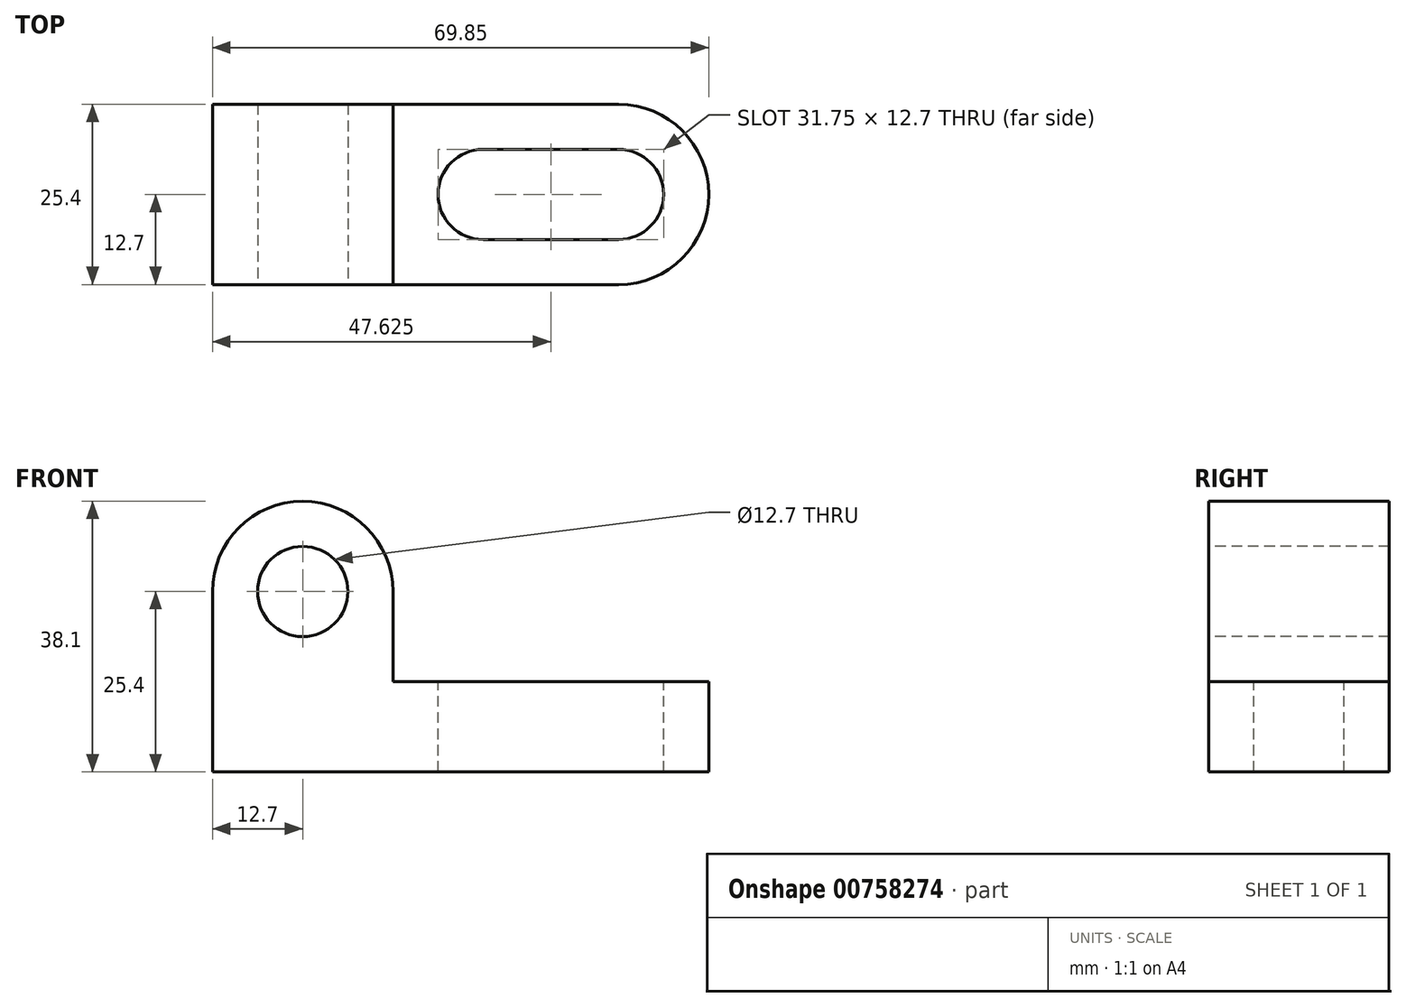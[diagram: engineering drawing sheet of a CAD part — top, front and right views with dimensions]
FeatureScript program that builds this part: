
annotation { "Feature Type Name" : "Feature", "Feature Type Description" : "" }
export const myFeature = defineFeature(function(context is Context, id is Id, definition is map)
    precondition{}
    {
        {
            var Q0;
            Q0=qCreatedBy(makeId("Front.planeOp"),FACE);
            var sketch = newSketch(context, id + "F0", { "sketchPlane" : qUnion([Q0])});
            skLineSegment(sketch, "E0", {"start": v(0, 0) * mm, "end": v(69.85, 0) * mm});
            skLineSegment(sketch, "E1", {"start": v(69.85, 0) * mm, "end": v(69.85, 38.1) * mm});
            skLineSegment(sketch, "E2", {"start": v(69.85, 38.1) * mm, "end": v(0, 38.1) * mm});
            skLineSegment(sketch, "E3", {"start": v(0, 38.1) * mm, "end": v(0, 0) * mm});
            skSolve(sketch);
        }
        {
            var Q0;
            Q0=makeQuery(id+"F0.imprint","IMPRINT",FACE,{"disambiguationData":[TD([[makeQuery(id+"F0.imprint","IMPRINT",EDGE,{"derivedFrom":sQuery(id+"F0.wireOp",EDGE,"E0")}),1.0]])]});
            extrude(context, id + "F1", {"entities" : qUnion([Q0]), "depth" : 25.4 * mm, "offsetDistance" : 25.4 * mm});
        }
        {
            var Q0;
            Q0=makeQuery(id+"F1.opExtrude","CAP_FACE",FACE,{"disambiguationData":[OSD([sQuery(id+"F0.wireOp",EDGE,"E0"),sQuery(id+"F0.wireOp",EDGE,"E1"),sQuery(id+"F0.wireOp",EDGE,"E2"),sQuery(id+"F0.wireOp",EDGE,"E3")])],"isStart":false});
            var sketch = newSketch(context, id + "F2", { "sketchPlane" : qUnion([Q0])});
            skLineSegment(sketch, "E4", {"start": v(25.4, 38.1) * mm, "end": v(25.4, 12.7) * mm});
            skLineSegment(sketch, "E5", {"start": v(25.4, 12.7) * mm, "end": v(69.85, 12.7) * mm});
            skSolve(sketch);
        }
        {
            var Q0;
            {var subQ0=sQuery(id+"F2.wireOp",EDGE,"E4");Q0=makeQuery(id+"F2.imprint","IMPRINT",FACE,{"disambiguationData":[TD([[makeQuery(id+"F2.imprint","IMPRINT",EDGE,{"derivedFrom":subQ0}),1.0]])]});}
            extrude(context, id + "F3", {"entities" : qUnion([Q0]), "operationType" : NewBodyOperationType.REMOVE, "oppositeDirection" : true, "depth" : 25.4 * mm, "offsetDistance" : 25.4 * mm});
        }
        {
            var Q0;
            Q0=makeQuery(id+"F3.boolean.opBoolean","COPY",FACE,{"derivedFrom":makeQuery(id+"F3.opExtrude","SWEPT_FACE",FACE,{"disambiguationData":[OSD([sQuery(id+"F2.wireOp",EDGE,"E5")])]})});
            var sketch = newSketch(context, id + "F4", { "sketchPlane" : qUnion([Q0])});
            skCircle(sketch, "E6", {"center": v(38.1, -12.7) * mm, "radius": 6.35 * mm});
            skPoint(sketch, "E6.centerSnap0", {"position": v(25.4, -12.7) * mm});
            skCircle(sketch, "E7", {"center": v(57.15, -12.7) * mm, "radius": 6.35 * mm});
            skLineSegment(sketch, "E8", {"start": v(38.1, -12.7) * mm, "end": v(38.1, -6.35) * mm});
            skLineSegment(sketch, "E9", {"start": v(38.1, -6.35) * mm, "end": v(57.15, -6.35) * mm});
            skLineSegment(sketch, "E10", {"start": v(57.15, -6.35) * mm, "end": v(57.15, -19.05) * mm});
            skLineSegment(sketch, "E11", {"start": v(57.15, -19.05) * mm, "end": v(38.1, -19.05) * mm});
            skLineSegment(sketch, "E12", {"start": v(38.1, -19.05) * mm, "end": v(38.1, -12.7) * mm});
            skSolve(sketch);
        }
        {
            var Q0;
            {var subQ0=sQuery(id+"F4.wireOp",EDGE,"E8");Q0=makeQuery(id+"F4.imprint","IMPRINT",FACE,{"disambiguationData":[TD([[makeQuery(id+"F4.imprint","IMPRINT",EDGE,{"derivedFrom":subQ0}),1.0]])]});}
            var Q1;
            {var subQ0=sQuery(id+"F4.wireOp",EDGE,"E8");Q1=makeQuery(id+"F4.imprint","IMPRINT",FACE,{"disambiguationData":[TD([[makeQuery(id+"F4.imprint","IMPRINT",EDGE,{"derivedFrom":subQ0}),-1.0]])]});}
            var Q2;
            {var subQ0=sQuery(id+"F4.wireOp",EDGE,"E9");Q2=makeQuery(id+"F4.imprint","IMPRINT",FACE,{"disambiguationData":[TD([[makeQuery(id+"F4.imprint","IMPRINT",EDGE,{"derivedFrom":subQ0}),-1.0]])]});}
            var Q3;
            {var subQ0=sQuery(id+"F4.wireOp",EDGE,"E10");Q3=makeQuery(id+"F4.imprint","IMPRINT",FACE,{"disambiguationData":[TD([[makeQuery(id+"F4.imprint","IMPRINT",EDGE,{"derivedFrom":subQ0}),1.0]])]});}
            var Q4;
            {var subQ0=sQuery(id+"F4.wireOp",EDGE,"E10");Q4=makeQuery(id+"F4.imprint","IMPRINT",FACE,{"disambiguationData":[TD([[makeQuery(id+"F4.imprint","IMPRINT",EDGE,{"derivedFrom":subQ0}),-1.0]])]});}
            extrude(context, id + "F5", {"entities" : qUnion([Q0, Q1, Q2, Q3, Q4]), "operationType" : NewBodyOperationType.REMOVE, "oppositeDirection" : true, "depth" : 12.7 * mm, "offsetDistance" : 25.4 * mm});
        }
        {
            var Q0;
            Q0=makeQuery(id+"F1.opExtrude","CAP_FACE",FACE,{"disambiguationData":[OSD([sQuery(id+"F0.wireOp",EDGE,"E0"),sQuery(id+"F0.wireOp",EDGE,"E1"),sQuery(id+"F0.wireOp",EDGE,"E2"),sQuery(id+"F0.wireOp",EDGE,"E3")])],"isStart":false});
            var sketch = newSketch(context, id + "F6", { "sketchPlane" : qUnion([Q0])});
            skCircle(sketch, "E13", {"center": v(12.7, 25.4) * mm, "radius": 6.35 * mm});
            skArc(sketch, "E14", {"start": v(25.4, 25.4) * mm, "mid": v(12.7, 38.1) * mm, "end": v(0, 25.4) * mm});
            skSolve(sketch);
        }
        {
            var Q0;
            Q0=makeQuery(id+"F6.imprint","IMPRINT",FACE,{"disambiguationData":[TD([[makeQuery(id+"F6.imprint","IMPRINT",EDGE,{"derivedFrom":sQuery(id+"F6.wireOp",EDGE,"E13")}),1.0]])]});
            var Q1;
            {var subQ0=sQuery(id+"F6.wireOp",EDGE,"E14");var subQ1=makeQuery(id+"F3.boolean.opBoolean","COPY",EDGE,{"derivedFrom":makeQuery(id+"F3.opExtrude","CAP_EDGE",EDGE,{"disambiguationData":[OSD([sQuery(id+"F2.wireOp",EDGE,"E4")])],"isStart":true})});var subQ2=makeQuery(id+"F6.imprint","INTERSECT",VERTEX,{"derivedFrom":[subQ1,subQ0]});Q1=makeQuery(id+"F6.imprint","IMPRINT",FACE,{"disambiguationData":[TD([[makeQuery(id+"F6.imprint","IMPRINT",EDGE,{"disambiguationData":[TD([[subQ2,-1.0]])],"derivedFrom":subQ0}),-1.0]])]});}
            var Q2;
            {var subQ0=sQuery(id+"F6.wireOp",EDGE,"E14");var subQ1=makeQuery(id+"F1.opExtrude","CAP_EDGE",EDGE,{"disambiguationData":[OSD([sQuery(id+"F0.wireOp",EDGE,"E3")])],"isStart":false});var subQ2=makeQuery(id+"F6.imprint","INTERSECT",VERTEX,{"derivedFrom":[subQ1,subQ0]});Q2=makeQuery(id+"F6.imprint","IMPRINT",FACE,{"disambiguationData":[TD([[makeQuery(id+"F6.imprint","IMPRINT",EDGE,{"disambiguationData":[TD([[subQ2,1.0]])],"derivedFrom":subQ0}),-1.0]])]});}
            extrude(context, id + "F7", {"entities" : qUnion([Q0, Q1, Q2]), "operationType" : NewBodyOperationType.REMOVE, "oppositeDirection" : true, "depth" : 25.4 * mm, "offsetDistance" : 25.4 * mm});
        }
        {
            var Q0;
            Q0=makeQuery(id+"F3.boolean.opBoolean","COPY",FACE,{"derivedFrom":makeQuery(id+"F3.opExtrude","SWEPT_FACE",FACE,{"disambiguationData":[OSD([sQuery(id+"F2.wireOp",EDGE,"E5")])]})});
            var sketch = newSketch(context, id + "F8", { "sketchPlane" : qUnion([Q0])});
            skArc(sketch, "E15", {"start": v(57.15, -25.4) * mm, "mid": v(69.85, -12.7) * mm, "end": v(57.15, 0) * mm});
            skSolve(sketch);
        }
        {
            var Q0;
            {var subQ0=sQuery(id+"F8.wireOp",EDGE,"E15");var subQ1=sQuery(id+"F2.wireOp",EDGE,"E5");var subQ2=makeQuery(id+"F3.boolean.opBoolean","COPY",EDGE,{"derivedFrom":makeQuery(id+"F3.opExtrude","CAP_EDGE",EDGE,{"disambiguationData":[OSD([subQ1])],"isStart":false})});var subQ3=makeQuery(id+"F8.imprint","INTERSECT",VERTEX,{"derivedFrom":[subQ2,subQ0]});Q0=makeQuery(id+"F8.imprint","IMPRINT",FACE,{"disambiguationData":[TD([[makeQuery(id+"F8.imprint","IMPRINT",EDGE,{"disambiguationData":[TD([[subQ3,1.0]])],"derivedFrom":subQ0}),-1.0]])]});}
            var Q1;
            {var subQ0=sQuery(id+"F8.wireOp",EDGE,"E15");var subQ1=sQuery(id+"F2.wireOp",EDGE,"E5");var subQ2=makeQuery(id+"F3.boolean.opBoolean","COPY",EDGE,{"derivedFrom":makeQuery(id+"F3.opExtrude","CAP_EDGE",EDGE,{"disambiguationData":[OSD([subQ1])],"isStart":true})});var subQ3=makeQuery(id+"F8.imprint","INTERSECT",VERTEX,{"derivedFrom":[subQ2,subQ0]});Q1=makeQuery(id+"F8.imprint","IMPRINT",FACE,{"disambiguationData":[TD([[makeQuery(id+"F8.imprint","IMPRINT",EDGE,{"disambiguationData":[TD([[subQ3,-1.0]])],"derivedFrom":subQ0}),-1.0]])]});}
            extrude(context, id + "F9", {"entities" : qUnion([Q0, Q1]), "operationType" : NewBodyOperationType.REMOVE, "oppositeDirection" : true, "depth" : 25.4 * mm, "offsetDistance" : 25.4 * mm});
        }
    });
